annotation { "Feature Type Name" : "Feature", "Feature Type Description" : "" }
export const myFeature = defineFeature(function(context is Context, id is Id, definition is map)
    precondition{}
    {
        {
            var Q0;
            Q0=qCreatedBy(makeId("Top.planeOp"),FACE);
            var sketch = newSketch(context, id + "F0", { "sketchPlane" : qUnion([Q0])});
            skLineSegment(sketch, "E0.bottom", {"start": v(-40.25, 43.5) * mm, "end": v(40.25, 43.5) * mm});
            skLineSegment(sketch, "E0.top", {"start": v(-40.25, -43.5) * mm, "end": v(40.25, -43.5) * mm});
            skLineSegment(sketch, "E0.left", {"start": v(-40.25, 43.5) * mm, "end": v(-40.25, -43.5) * mm});
            skLineSegment(sketch, "E0.right", {"start": v(40.25, 43.5) * mm, "end": v(40.25, -43.5) * mm});
            skSolve(sketch);
        }
        {
            var Q0;
            Q0=qCreatedBy(makeId("Top.planeOp"),FACE);
            var sketch = newSketch(context, id + "F1", { "sketchPlane" : qUnion([Q0])});
            skText(sketch, "E1", { "text": "Toms Cafe", "fontName": "OpenSans-Bold.ttf"});
            skLineSegment(sketch, "E2", {"start": v(-25, -33.55) * mm, "end": v(-40.25, -33.55) * mm, "construction": true});
            skLineSegment(sketch, "E3", {"start": v(25, -33.55) * mm, "end": v(40.25, -33.55) * mm, "construction": true});
            skPoint(sketch, "E4.oppositeSnap0", {"position": v(-32.62, -33.55) * mm});
            skLineSegment(sketch, "E5.bottom", {"start": v(11.82, -37.2) * mm, "end": v(12.9, -37.2) * mm});
            skLineSegment(sketch, "E5.top", {"start": v(11.82, -38.83) * mm, "end": v(12.9, -38.83) * mm});
            skLineSegment(sketch, "E5.left", {"start": v(11.82, -37.2) * mm, "end": v(11.82, -38.83) * mm});
            skLineSegment(sketch, "E5.right", {"start": v(12.9, -37.2) * mm, "end": v(12.9, -38.83) * mm});
            skLineSegment(sketch, "E6.bottom", {"start": v(11.92, -34.98) * mm, "end": v(12.9, -34.98) * mm});
            skLineSegment(sketch, "E6.top", {"start": v(11.92, -36.37) * mm, "end": v(12.9, -36.37) * mm});
            skLineSegment(sketch, "E6.left", {"start": v(11.92, -34.98) * mm, "end": v(11.92, -36.37) * mm});
            skLineSegment(sketch, "E6.right", {"start": v(12.9, -34.98) * mm, "end": v(12.9, -36.37) * mm});
            skLineSegment(sketch, "E7", {"start": v(-39.23, 0) * mm, "end": v(38.52, 0) * mm, "construction": true});
            skCircle(sketch, "E8", {"center": v(-34.75, 38) * mm, "radius": 2.5 * mm});
            skCircle(sketch, "E9", {"center": v(-27.82, 34) * mm, "radius": 2.5 * mm});
            skCircle(sketch, "E10", {"center": v(-34.75, 30) * mm, "radius": 2.5 * mm});
            skCircle(sketch, "E11", {"center": v(-27.82, 26) * mm, "radius": 2.5 * mm});
            skCircle(sketch, "E12.0.1.0", {"center": v(-27.82, 18) * mm, "radius": 2.5 * mm});
            skCircle(sketch, "E12.0.1.1", {"center": v(-34.75, 22) * mm, "radius": 2.5 * mm});
            skCircle(sketch, "E12.0.1.2", {"center": v(-34.75, 14) * mm, "radius": 2.5 * mm});
            skCircle(sketch, "E12.0.1.3", {"center": v(-27.82, 10) * mm, "radius": 2.5 * mm});
            skCircle(sketch, "E12.0.2.0", {"center": v(-27.82, 2) * mm, "radius": 2.5 * mm});
            skCircle(sketch, "E12.0.2.1", {"center": v(-34.75, 6) * mm, "radius": 2.5 * mm});
            skCircle(sketch, "E12.0.2.2", {"center": v(-34.75, -2) * mm, "radius": 2.5 * mm});
            skCircle(sketch, "E12.0.2.3", {"center": v(-27.82, -6) * mm, "radius": 2.5 * mm});
            skCircle(sketch, "E12.0.3.0", {"center": v(-27.82, -14) * mm, "radius": 2.5 * mm});
            skCircle(sketch, "E12.0.3.1", {"center": v(-34.75, -10) * mm, "radius": 2.5 * mm});
            skCircle(sketch, "E12.0.3.2", {"center": v(-34.75, -18) * mm, "radius": 2.5 * mm});
            skCircle(sketch, "E12.0.3.3", {"center": v(-27.82, -22) * mm, "radius": 2.5 * mm});
            skCircle(sketch, "E12.0.4.0", {"center": v(-27.82, -30) * mm, "radius": 2.5 * mm});
            skCircle(sketch, "E12.0.4.1", {"center": v(-34.75, -26) * mm, "radius": 2.5 * mm});
            skCircle(sketch, "E12.0.4.2", {"center": v(-34.75, -34) * mm, "radius": 2.5 * mm});
            skCircle(sketch, "E12.1.0.0", {"center": v(-13.97, 34) * mm, "radius": 2.5 * mm});
            skCircle(sketch, "E12.1.0.1", {"center": v(-20.9, 38) * mm, "radius": 2.5 * mm});
            skCircle(sketch, "E12.1.0.2", {"center": v(-20.9, 30) * mm, "radius": 2.5 * mm});
            skCircle(sketch, "E12.1.0.3", {"center": v(-13.97, 26) * mm, "radius": 2.5 * mm});
            skCircle(sketch, "E12.1.1.0", {"center": v(-13.97, 18) * mm, "radius": 2.5 * mm});
            skCircle(sketch, "E12.1.1.1", {"center": v(-20.9, 22) * mm, "radius": 2.5 * mm});
            skCircle(sketch, "E12.1.1.2", {"center": v(-20.9, 14) * mm, "radius": 2.5 * mm});
            skCircle(sketch, "E12.1.1.3", {"center": v(-13.97, 10) * mm, "radius": 2.5 * mm});
            skCircle(sketch, "E12.1.2.0", {"center": v(-13.97, 2) * mm, "radius": 2.5 * mm});
            skCircle(sketch, "E12.1.2.1", {"center": v(-20.9, 6) * mm, "radius": 2.5 * mm});
            skCircle(sketch, "E12.1.2.2", {"center": v(-20.9, -2) * mm, "radius": 2.5 * mm});
            skCircle(sketch, "E12.1.2.3", {"center": v(-13.97, -6) * mm, "radius": 2.5 * mm});
            skCircle(sketch, "E12.1.3.0", {"center": v(-13.97, -14) * mm, "radius": 2.5 * mm});
            skCircle(sketch, "E12.1.3.1", {"center": v(-20.9, -10) * mm, "radius": 2.5 * mm});
            skCircle(sketch, "E12.1.3.2", {"center": v(-20.9, -18) * mm, "radius": 2.5 * mm});
            skCircle(sketch, "E12.1.3.3", {"center": v(-13.97, -22) * mm, "radius": 2.5 * mm});
            skCircle(sketch, "E12.1.4.0", {"center": v(-13.97, -30) * mm, "radius": 2.5 * mm});
            skCircle(sketch, "E12.1.4.1", {"center": v(-20.9, -26) * mm, "radius": 2.5 * mm});
            skCircle(sketch, "E12.2.0.0", {"center": v(-0.1, 34) * mm, "radius": 2.5 * mm});
            skCircle(sketch, "E12.2.0.1", {"center": v(-7.04, 38) * mm, "radius": 2.5 * mm});
            skCircle(sketch, "E12.2.0.2", {"center": v(-7.04, 30) * mm, "radius": 2.5 * mm});
            skCircle(sketch, "E12.2.0.3", {"center": v(-0.1, 26) * mm, "radius": 2.5 * mm});
            skCircle(sketch, "E12.2.1.0", {"center": v(-0.1, 18) * mm, "radius": 2.5 * mm});
            skCircle(sketch, "E12.2.1.1", {"center": v(-7.04, 22) * mm, "radius": 2.5 * mm});
            skCircle(sketch, "E12.2.1.2", {"center": v(-7.04, 14) * mm, "radius": 2.5 * mm});
            skCircle(sketch, "E12.2.1.3", {"center": v(-0.1, 10) * mm, "radius": 2.5 * mm});
            skCircle(sketch, "E12.2.2.0", {"center": v(-0.1, 2) * mm, "radius": 2.5 * mm});
            skCircle(sketch, "E12.2.2.1", {"center": v(-7.04, 6) * mm, "radius": 2.5 * mm});
            skCircle(sketch, "E12.2.2.2", {"center": v(-7.04, -2) * mm, "radius": 2.5 * mm});
            skCircle(sketch, "E12.2.2.3", {"center": v(-0.1, -6) * mm, "radius": 2.5 * mm});
            skCircle(sketch, "E12.2.3.0", {"center": v(-0.1, -14) * mm, "radius": 2.5 * mm});
            skCircle(sketch, "E12.2.3.1", {"center": v(-7.04, -10) * mm, "radius": 2.5 * mm});
            skCircle(sketch, "E12.2.3.2", {"center": v(-7.04, -18) * mm, "radius": 2.5 * mm});
            skCircle(sketch, "E12.2.3.3", {"center": v(-0.1, -22) * mm, "radius": 2.5 * mm});
            skCircle(sketch, "E12.2.4.0", {"center": v(-0.1, -30) * mm, "radius": 2.5 * mm});
            skCircle(sketch, "E12.2.4.1", {"center": v(-7.04, -26) * mm, "radius": 2.5 * mm});
            skCircle(sketch, "E12.3.0.0", {"center": v(13.75, 34) * mm, "radius": 2.5 * mm});
            skCircle(sketch, "E12.3.0.1", {"center": v(6.82, 38) * mm, "radius": 2.5 * mm});
            skCircle(sketch, "E12.3.0.2", {"center": v(6.82, 30) * mm, "radius": 2.5 * mm});
            skCircle(sketch, "E12.3.0.3", {"center": v(13.75, 26) * mm, "radius": 2.5 * mm});
            skCircle(sketch, "E12.3.1.0", {"center": v(13.75, 18) * mm, "radius": 2.5 * mm});
            skCircle(sketch, "E12.3.1.1", {"center": v(6.82, 22) * mm, "radius": 2.5 * mm});
            skCircle(sketch, "E12.3.1.2", {"center": v(6.82, 14) * mm, "radius": 2.5 * mm});
            skCircle(sketch, "E12.3.1.3", {"center": v(13.75, 10) * mm, "radius": 2.5 * mm});
            skCircle(sketch, "E12.3.2.0", {"center": v(13.75, 2) * mm, "radius": 2.5 * mm});
            skCircle(sketch, "E12.3.2.1", {"center": v(6.82, 6) * mm, "radius": 2.5 * mm});
            skCircle(sketch, "E12.3.2.2", {"center": v(6.82, -2) * mm, "radius": 2.5 * mm});
            skCircle(sketch, "E12.3.2.3", {"center": v(13.75, -6) * mm, "radius": 2.5 * mm});
            skCircle(sketch, "E12.3.3.0", {"center": v(13.75, -14) * mm, "radius": 2.5 * mm});
            skCircle(sketch, "E12.3.3.1", {"center": v(6.82, -10) * mm, "radius": 2.5 * mm});
            skCircle(sketch, "E12.3.3.2", {"center": v(6.82, -18) * mm, "radius": 2.5 * mm});
            skCircle(sketch, "E12.3.3.3", {"center": v(13.75, -22) * mm, "radius": 2.5 * mm});
            skCircle(sketch, "E12.3.4.0", {"center": v(13.75, -30) * mm, "radius": 2.5 * mm});
            skCircle(sketch, "E12.3.4.1", {"center": v(6.82, -26) * mm, "radius": 2.5 * mm});
            skCircle(sketch, "E12.4.0.0", {"center": v(27.6, 34) * mm, "radius": 2.5 * mm});
            skCircle(sketch, "E12.4.0.1", {"center": v(20.67, 38) * mm, "radius": 2.5 * mm});
            skCircle(sketch, "E12.4.0.2", {"center": v(20.67, 30) * mm, "radius": 2.5 * mm});
            skCircle(sketch, "E12.4.0.3", {"center": v(27.6, 26) * mm, "radius": 2.5 * mm});
            skCircle(sketch, "E12.4.1.0", {"center": v(27.6, 18) * mm, "radius": 2.5 * mm});
            skCircle(sketch, "E12.4.1.1", {"center": v(20.67, 22) * mm, "radius": 2.5 * mm});
            skCircle(sketch, "E12.4.1.2", {"center": v(20.67, 14) * mm, "radius": 2.5 * mm});
            skCircle(sketch, "E12.4.1.3", {"center": v(27.6, 10) * mm, "radius": 2.5 * mm});
            skCircle(sketch, "E12.4.2.0", {"center": v(27.6, 2) * mm, "radius": 2.5 * mm});
            skCircle(sketch, "E12.4.2.1", {"center": v(20.67, 6) * mm, "radius": 2.5 * mm});
            skCircle(sketch, "E12.4.2.2", {"center": v(20.67, -2) * mm, "radius": 2.5 * mm});
            skCircle(sketch, "E12.4.2.3", {"center": v(27.6, -6) * mm, "radius": 2.5 * mm});
            skCircle(sketch, "E12.4.3.0", {"center": v(27.6, -14) * mm, "radius": 2.5 * mm});
            skCircle(sketch, "E12.4.3.1", {"center": v(20.67, -10) * mm, "radius": 2.5 * mm});
            skCircle(sketch, "E12.4.3.2", {"center": v(20.67, -18) * mm, "radius": 2.5 * mm});
            skCircle(sketch, "E12.4.3.3", {"center": v(27.6, -22) * mm, "radius": 2.5 * mm});
            skCircle(sketch, "E12.4.4.0", {"center": v(27.6, -30) * mm, "radius": 2.5 * mm});
            skCircle(sketch, "E12.4.4.1", {"center": v(20.67, -26) * mm, "radius": 2.5 * mm});
            skCircle(sketch, "E12.5.0.1", {"center": v(34.53, 38) * mm, "radius": 2.5 * mm});
            skCircle(sketch, "E12.5.0.2", {"center": v(34.53, 30) * mm, "radius": 2.5 * mm});
            skCircle(sketch, "E12.5.1.1", {"center": v(34.53, 22) * mm, "radius": 2.5 * mm});
            skCircle(sketch, "E12.5.1.2", {"center": v(34.53, 14) * mm, "radius": 2.5 * mm});
            skCircle(sketch, "E12.5.2.1", {"center": v(34.53, 6) * mm, "radius": 2.5 * mm});
            skCircle(sketch, "E12.5.2.2", {"center": v(34.53, -2) * mm, "radius": 2.5 * mm});
            skCircle(sketch, "E12.5.3.1", {"center": v(34.53, -10) * mm, "radius": 2.5 * mm});
            skCircle(sketch, "E12.5.3.2", {"center": v(34.53, -18) * mm, "radius": 2.5 * mm});
            skCircle(sketch, "E12.5.4.1", {"center": v(34.53, -26) * mm, "radius": 2.5 * mm});
            skCircle(sketch, "E12.5.4.2", {"center": v(34.53, -34) * mm, "radius": 2.5 * mm});
            skLineSegment(sketch, "E12.direction1", {"start": v(-34.75, 30) * mm, "end": v(-20.9, 30) * mm, "construction": true});
            skLineSegment(sketch, "E12.direction2", {"start": v(-34.75, 30) * mm, "end": v(-34.75, 14) * mm, "construction": true});
            skLineSegment(sketch, "E13", {"start": v(-37.03, 39.03) * mm, "end": v(-40.25, 39.03) * mm, "construction": true});
            skLineSegment(sketch, "E14", {"start": v(37.03, 38) * mm, "end": v(40.25, 38) * mm, "construction": true});
            skLineSegment(sketch, "E15.bottom", {"start": v(-40.25, -43.5) * mm, "end": v(40.25, -43.5) * mm});
            skLineSegment(sketch, "E15.top", {"start": v(-40.25, 43.5) * mm, "end": v(40.25, 43.5) * mm});
            skLineSegment(sketch, "E15.left", {"start": v(-40.25, -43.5) * mm, "end": v(-40.25, 43.5) * mm});
            skLineSegment(sketch, "E15.right", {"start": v(40.25, -43.5) * mm, "end": v(40.25, 43.5) * mm});
            const initialGuessF1  = {"E1": [-0.025, -0.0405, 1, 0, 0.00695]};
            skSetInitialGuess(sketch, initialGuessF1);
            skSolve(sketch);
        }
        {
            var Q0;
            Q0 = qSketchRegion(id + "F1", true);
            extrude(context, id + "F2", {"entities" : qUnion([Q0]), "depth" : 3 * mm, "offsetDistance" : 25 * mm});
        }
        {
            var Q0;
            Q0=makeQuery(id+"F2.opExtrude","CAP_EDGE",EDGE,{"disambiguationData":[OSD([sQuery(id+"F1.wireOp",EDGE,"E15.bottom")])],"isStart":false});
            var Q1;
            Q1=makeQuery(id+"F2.opExtrude","CAP_EDGE",EDGE,{"disambiguationData":[OSD([sQuery(id+"F1.wireOp",EDGE,"E15.left")])],"isStart":false});
            var Q2;
            Q2=makeQuery(id+"F2.opExtrude","CAP_EDGE",EDGE,{"disambiguationData":[OSD([sQuery(id+"F1.wireOp",EDGE,"E15.top")])],"isStart":false});
            var Q3;
            Q3=makeQuery(id+"F2.opExtrude","CAP_EDGE",EDGE,{"disambiguationData":[OSD([sQuery(id+"F1.wireOp",EDGE,"E15.right")])],"isStart":false});
            var Q4;
            Q4=makeQuery(id+"F2.opExtrude","CAP_EDGE",EDGE,{"disambiguationData":[OSD([sQuery(id+"F1.wireOp",EDGE,"E12.0.4.2")])],"isStart":false});
            var Q5;
            Q5=makeQuery(id+"F2.opExtrude","CAP_EDGE",EDGE,{"disambiguationData":[OSD([sQuery(id+"F1.wireOp",EDGE,"E12.0.4.0")])],"isStart":false});
            var Q6;
            Q6=makeQuery(id+"F2.opExtrude","CAP_EDGE",EDGE,{"disambiguationData":[OSD([sQuery(id+"F1.wireOp",EDGE,"E12.0.4.1")])],"isStart":false});
            var Q7;
            Q7=makeQuery(id+"F2.opExtrude","CAP_EDGE",EDGE,{"disambiguationData":[OSD([sQuery(id+"F1.wireOp",EDGE,"E12.0.3.3")])],"isStart":false});
            var Q8;
            Q8=makeQuery(id+"F2.opExtrude","SWEPT_FACE",FACE,{"disambiguationData":[OSD([sQuery(id+"F1.wireOp",EDGE,"E12.0.3.2")])]});
            var Q9;
            Q9=makeQuery(id+"F2.opExtrude","CAP_EDGE",EDGE,{"disambiguationData":[OSD([sQuery(id+"F1.wireOp",EDGE,"E12.0.3.1")])],"isStart":false});
            var Q10;
            Q10=makeQuery(id+"F2.opExtrude","CAP_EDGE",EDGE,{"disambiguationData":[OSD([sQuery(id+"F1.wireOp",EDGE,"E12.0.2.3")])],"isStart":false});
            var Q11;
            Q11=makeQuery(id+"F2.opExtrude","CAP_EDGE",EDGE,{"disambiguationData":[OSD([sQuery(id+"F1.wireOp",EDGE,"E12.0.2.2")])],"isStart":false});
            var Q12;
            Q12=makeQuery(id+"F2.opExtrude","CAP_EDGE",EDGE,{"disambiguationData":[OSD([sQuery(id+"F1.wireOp",EDGE,"E12.0.2.1")])],"isStart":false});
            var Q13;
            Q13=makeQuery(id+"F2.opExtrude","CAP_EDGE",EDGE,{"disambiguationData":[OSD([sQuery(id+"F1.wireOp",EDGE,"E12.0.2.0")])],"isStart":false});
            var Q14;
            Q14=makeQuery(id+"F2.opExtrude","CAP_EDGE",EDGE,{"disambiguationData":[OSD([sQuery(id+"F1.wireOp",EDGE,"E12.0.1.3")])],"isStart":false});
            var Q15;
            Q15=makeQuery(id+"F2.opExtrude","CAP_EDGE",EDGE,{"disambiguationData":[OSD([sQuery(id+"F1.wireOp",EDGE,"E12.0.1.2")])],"isStart":false});
            var Q16;
            Q16=makeQuery(id+"F2.opExtrude","CAP_EDGE",EDGE,{"disambiguationData":[OSD([sQuery(id+"F1.wireOp",EDGE,"E12.0.1.1")])],"isStart":false});
            var Q17;
            Q17=makeQuery(id+"F2.opExtrude","CAP_EDGE",EDGE,{"disambiguationData":[OSD([sQuery(id+"F1.wireOp",EDGE,"E10")])],"isStart":false});
            var Q18;
            Q18=makeQuery(id+"F2.opExtrude","CAP_EDGE",EDGE,{"disambiguationData":[OSD([sQuery(id+"F1.wireOp",EDGE,"E8")])],"isStart":false});
            var Q19;
            Q19=makeQuery(id+"F2.opExtrude","CAP_EDGE",EDGE,{"disambiguationData":[OSD([sQuery(id+"F1.wireOp",EDGE,"E12.0.1.0")])],"isStart":false});
            var Q20;
            Q20=makeQuery(id+"F2.opExtrude","CAP_EDGE",EDGE,{"disambiguationData":[OSD([sQuery(id+"F1.wireOp",EDGE,"E12.0.3.0")])],"isStart":false});
            var Q21;
            Q21=makeQuery(id+"F2.opExtrude","CAP_EDGE",EDGE,{"disambiguationData":[OSD([sQuery(id+"F1.wireOp",EDGE,"E11")])],"isStart":false});
            var Q22;
            Q22=makeQuery(id+"F2.opExtrude","CAP_EDGE",EDGE,{"disambiguationData":[OSD([sQuery(id+"F1.wireOp",EDGE,"E9")])],"isStart":false});
            var Q23;
            Q23=makeQuery(id+"F2.opExtrude","CAP_EDGE",EDGE,{"disambiguationData":[OSD([sQuery(id+"F1.wireOp",EDGE,"E12.1.0.1")])],"isStart":false});
            var Q24;
            Q24=makeQuery(id+"F2.opExtrude","CAP_EDGE",EDGE,{"disambiguationData":[OSD([sQuery(id+"F1.wireOp",EDGE,"E12.1.0.2")])],"isStart":false});
            var Q25;
            Q25=makeQuery(id+"F2.opExtrude","CAP_EDGE",EDGE,{"disambiguationData":[OSD([sQuery(id+"F1.wireOp",EDGE,"E12.1.1.1")])],"isStart":false});
            var Q26;
            Q26=makeQuery(id+"F2.opExtrude","CAP_EDGE",EDGE,{"disambiguationData":[OSD([sQuery(id+"F1.wireOp",EDGE,"E12.1.1.2")])],"isStart":false});
            var Q27;
            Q27=makeQuery(id+"F2.opExtrude","CAP_EDGE",EDGE,{"disambiguationData":[OSD([sQuery(id+"F1.wireOp",EDGE,"E12.1.2.1")])],"isStart":false});
            var Q28;
            Q28=makeQuery(id+"F2.opExtrude","CAP_EDGE",EDGE,{"disambiguationData":[OSD([sQuery(id+"F1.wireOp",EDGE,"E12.1.2.2")])],"isStart":false});
            var Q29;
            Q29=makeQuery(id+"F2.opExtrude","CAP_EDGE",EDGE,{"disambiguationData":[OSD([sQuery(id+"F1.wireOp",EDGE,"E12.1.3.1")])],"isStart":false});
            var Q30;
            Q30=makeQuery(id+"F2.opExtrude","CAP_EDGE",EDGE,{"disambiguationData":[OSD([sQuery(id+"F1.wireOp",EDGE,"E12.1.3.2")])],"isStart":false});
            var Q31;
            Q31=makeQuery(id+"F2.opExtrude","CAP_EDGE",EDGE,{"disambiguationData":[OSD([sQuery(id+"F1.wireOp",EDGE,"E12.1.4.1")])],"isStart":false});
            var Q32;
            Q32=makeQuery(id+"F2.opExtrude","CAP_EDGE",EDGE,{"disambiguationData":[OSD([sQuery(id+"F1.wireOp",EDGE,"E12.1.0.0")])],"isStart":false});
            var Q33;
            Q33=makeQuery(id+"F2.opExtrude","CAP_EDGE",EDGE,{"disambiguationData":[OSD([sQuery(id+"F1.wireOp",EDGE,"E12.1.0.3")])],"isStart":false});
            var Q34;
            Q34=makeQuery(id+"F2.opExtrude","CAP_EDGE",EDGE,{"disambiguationData":[OSD([sQuery(id+"F1.wireOp",EDGE,"E12.1.1.0")])],"isStart":false});
            var Q35;
            Q35=makeQuery(id+"F2.opExtrude","CAP_EDGE",EDGE,{"disambiguationData":[OSD([sQuery(id+"F1.wireOp",EDGE,"E12.1.1.3")])],"isStart":false});
            var Q36;
            Q36=makeQuery(id+"F2.opExtrude","CAP_EDGE",EDGE,{"disambiguationData":[OSD([sQuery(id+"F1.wireOp",EDGE,"E12.1.2.0")])],"isStart":false});
            var Q37;
            Q37=makeQuery(id+"F2.opExtrude","CAP_EDGE",EDGE,{"disambiguationData":[OSD([sQuery(id+"F1.wireOp",EDGE,"E12.1.2.3")])],"isStart":false});
            var Q38;
            Q38=makeQuery(id+"F2.opExtrude","CAP_EDGE",EDGE,{"disambiguationData":[OSD([sQuery(id+"F1.wireOp",EDGE,"E12.1.3.0")])],"isStart":false});
            var Q39;
            Q39=makeQuery(id+"F2.opExtrude","CAP_EDGE",EDGE,{"disambiguationData":[OSD([sQuery(id+"F1.wireOp",EDGE,"E12.1.3.3")])],"isStart":false});
            var Q40;
            Q40=makeQuery(id+"F2.opExtrude","CAP_EDGE",EDGE,{"disambiguationData":[OSD([sQuery(id+"F1.wireOp",EDGE,"E12.1.4.0")])],"isStart":false});
            var Q41;
            Q41=makeQuery(id+"F2.opExtrude","CAP_EDGE",EDGE,{"disambiguationData":[OSD([sQuery(id+"F1.wireOp",EDGE,"E12.2.4.1")])],"isStart":false});
            var Q42;
            Q42=makeQuery(id+"F2.opExtrude","CAP_EDGE",EDGE,{"disambiguationData":[OSD([sQuery(id+"F1.wireOp",EDGE,"E12.2.3.2")])],"isStart":false});
            var Q43;
            Q43=makeQuery(id+"F2.opExtrude","CAP_EDGE",EDGE,{"disambiguationData":[OSD([sQuery(id+"F1.wireOp",EDGE,"E12.2.3.1")])],"isStart":false});
            var Q44;
            Q44=makeQuery(id+"F2.opExtrude","CAP_EDGE",EDGE,{"disambiguationData":[OSD([sQuery(id+"F1.wireOp",EDGE,"E12.2.2.1")])],"isStart":false});
            var Q45;
            Q45=makeQuery(id+"F2.opExtrude","CAP_EDGE",EDGE,{"disambiguationData":[OSD([sQuery(id+"F1.wireOp",EDGE,"E12.2.1.2")])],"isStart":false});
            var Q46;
            Q46=makeQuery(id+"F2.opExtrude","CAP_EDGE",EDGE,{"disambiguationData":[OSD([sQuery(id+"F1.wireOp",EDGE,"E12.2.1.1")])],"isStart":false});
            var Q47;
            Q47=makeQuery(id+"F2.opExtrude","CAP_EDGE",EDGE,{"disambiguationData":[OSD([sQuery(id+"F1.wireOp",EDGE,"E12.2.0.2")])],"isStart":false});
            var Q48;
            Q48=makeQuery(id+"F2.opExtrude","CAP_EDGE",EDGE,{"disambiguationData":[OSD([sQuery(id+"F1.wireOp",EDGE,"E12.2.0.1")])],"isStart":false});
            var Q49;
            Q49=makeQuery(id+"F2.opExtrude","CAP_EDGE",EDGE,{"disambiguationData":[OSD([sQuery(id+"F1.wireOp",EDGE,"E12.2.0.0")])],"isStart":false});
            var Q50;
            Q50=makeQuery(id+"F2.opExtrude","CAP_EDGE",EDGE,{"disambiguationData":[OSD([sQuery(id+"F1.wireOp",EDGE,"E12.2.0.3")])],"isStart":false});
            var Q51;
            Q51=makeQuery(id+"F2.opExtrude","CAP_EDGE",EDGE,{"disambiguationData":[OSD([sQuery(id+"F1.wireOp",EDGE,"E12.2.1.0")])],"isStart":false});
            var Q52;
            Q52=makeQuery(id+"F2.opExtrude","CAP_EDGE",EDGE,{"disambiguationData":[OSD([sQuery(id+"F1.wireOp",EDGE,"E12.2.1.3")])],"isStart":false});
            var Q53;
            Q53=makeQuery(id+"F2.opExtrude","CAP_EDGE",EDGE,{"disambiguationData":[OSD([sQuery(id+"F1.wireOp",EDGE,"E12.2.2.0")])],"isStart":false});
            var Q54;
            Q54=makeQuery(id+"F2.opExtrude","CAP_EDGE",EDGE,{"disambiguationData":[OSD([sQuery(id+"F1.wireOp",EDGE,"E12.2.2.2")])],"isStart":false});
            var Q55;
            Q55=makeQuery(id+"F2.opExtrude","CAP_EDGE",EDGE,{"disambiguationData":[OSD([sQuery(id+"F1.wireOp",EDGE,"E12.2.2.3")])],"isStart":false});
            var Q56;
            Q56=makeQuery(id+"F2.opExtrude","CAP_EDGE",EDGE,{"disambiguationData":[OSD([sQuery(id+"F1.wireOp",EDGE,"E12.2.3.0")])],"isStart":false});
            var Q57;
            Q57=makeQuery(id+"F2.opExtrude","CAP_EDGE",EDGE,{"disambiguationData":[OSD([sQuery(id+"F1.wireOp",EDGE,"E12.2.3.3")])],"isStart":false});
            var Q58;
            Q58=makeQuery(id+"F2.opExtrude","CAP_EDGE",EDGE,{"disambiguationData":[OSD([sQuery(id+"F1.wireOp",EDGE,"E12.2.4.0")])],"isStart":false});
            var Q59;
            Q59=makeQuery(id+"F2.opExtrude","CAP_EDGE",EDGE,{"disambiguationData":[OSD([sQuery(id+"F1.wireOp",EDGE,"E12.3.0.1")])],"isStart":false});
            var Q60;
            Q60=makeQuery(id+"F2.opExtrude","CAP_EDGE",EDGE,{"disambiguationData":[OSD([sQuery(id+"F1.wireOp",EDGE,"E12.3.0.2")])],"isStart":false});
            chamfer(context, id + "F3", {"entities" : qUnion([Q0, Q1, Q2, Q3, Q4, Q5, Q6, Q7, Q8, Q9, Q10, Q11, Q12, Q13, Q14, Q15, Q16, Q17, Q18, Q19, Q20, Q21, Q22, Q23, Q24, Q25, Q26, Q27, Q28, Q29, Q30, Q31, Q32, Q33, Q34, Q35, Q36, Q37, Q38, Q39, Q40, Q41, Q42, Q43, Q44, Q45, Q46, Q47, Q48, Q49, Q50, Q51, Q52, Q53, Q54, Q55, Q56, Q57, Q58, Q59, Q60]), "width" : 1 * mm, "tangentPropagation" : true});
        }
        {
            var Q0;
            Q0=makeQuery(id+"F2.opExtrude","CAP_EDGE",EDGE,{"disambiguationData":[OSD([sQuery(id+"F1.wireOp",EDGE,"E12.3.1.1")])],"isStart":false});
            var Q1;
            Q1=makeQuery(id+"F2.opExtrude","CAP_EDGE",EDGE,{"disambiguationData":[OSD([sQuery(id+"F1.wireOp",EDGE,"E12.3.1.2")])],"isStart":false});
            var Q2;
            Q2=makeQuery(id+"F2.opExtrude","CAP_EDGE",EDGE,{"disambiguationData":[OSD([sQuery(id+"F1.wireOp",EDGE,"E12.3.2.1")])],"isStart":false});
            var Q3;
            Q3=makeQuery(id+"F2.opExtrude","CAP_EDGE",EDGE,{"disambiguationData":[OSD([sQuery(id+"F1.wireOp",EDGE,"E12.3.2.2")])],"isStart":false});
            var Q4;
            Q4=makeQuery(id+"F2.opExtrude","CAP_EDGE",EDGE,{"disambiguationData":[OSD([sQuery(id+"F1.wireOp",EDGE,"E12.3.3.1")])],"isStart":false});
            var Q5;
            Q5=makeQuery(id+"F2.opExtrude","CAP_EDGE",EDGE,{"disambiguationData":[OSD([sQuery(id+"F1.wireOp",EDGE,"E12.3.3.2")])],"isStart":false});
            var Q6;
            Q6=makeQuery(id+"F2.opExtrude","CAP_EDGE",EDGE,{"disambiguationData":[OSD([sQuery(id+"F1.wireOp",EDGE,"E12.3.4.1")])],"isStart":false});
            var Q7;
            Q7=makeQuery(id+"F2.opExtrude","CAP_EDGE",EDGE,{"disambiguationData":[OSD([sQuery(id+"F1.wireOp",EDGE,"E12.3.4.0")])],"isStart":false});
            var Q8;
            Q8=makeQuery(id+"F2.opExtrude","CAP_EDGE",EDGE,{"disambiguationData":[OSD([sQuery(id+"F1.wireOp",EDGE,"E12.3.3.3")])],"isStart":false});
            var Q9;
            Q9=makeQuery(id+"F2.opExtrude","CAP_EDGE",EDGE,{"disambiguationData":[OSD([sQuery(id+"F1.wireOp",EDGE,"E12.3.3.0")])],"isStart":false});
            var Q10;
            Q10=makeQuery(id+"F2.opExtrude","CAP_EDGE",EDGE,{"disambiguationData":[OSD([sQuery(id+"F1.wireOp",EDGE,"E12.3.2.3")])],"isStart":false});
            var Q11;
            Q11=makeQuery(id+"F2.opExtrude","CAP_EDGE",EDGE,{"disambiguationData":[OSD([sQuery(id+"F1.wireOp",EDGE,"E12.3.2.0")])],"isStart":false});
            var Q12;
            Q12=makeQuery(id+"F2.opExtrude","CAP_EDGE",EDGE,{"disambiguationData":[OSD([sQuery(id+"F1.wireOp",EDGE,"E12.3.1.3")])],"isStart":false});
            var Q13;
            Q13=makeQuery(id+"F2.opExtrude","CAP_EDGE",EDGE,{"disambiguationData":[OSD([sQuery(id+"F1.wireOp",EDGE,"E12.3.1.0")])],"isStart":false});
            var Q14;
            Q14=makeQuery(id+"F2.opExtrude","CAP_EDGE",EDGE,{"disambiguationData":[OSD([sQuery(id+"F1.wireOp",EDGE,"E12.3.0.3")])],"isStart":false});
            var Q15;
            Q15=makeQuery(id+"F2.opExtrude","CAP_EDGE",EDGE,{"disambiguationData":[OSD([sQuery(id+"F1.wireOp",EDGE,"E12.3.0.0")])],"isStart":false});
            var Q16;
            Q16=makeQuery(id+"F2.opExtrude","CAP_EDGE",EDGE,{"disambiguationData":[OSD([sQuery(id+"F1.wireOp",EDGE,"E12.4.0.1")])],"isStart":false});
            var Q17;
            Q17=makeQuery(id+"F2.opExtrude","CAP_EDGE",EDGE,{"disambiguationData":[OSD([sQuery(id+"F1.wireOp",EDGE,"E12.4.0.2")])],"isStart":false});
            var Q18;
            Q18=makeQuery(id+"F2.opExtrude","CAP_EDGE",EDGE,{"disambiguationData":[OSD([sQuery(id+"F1.wireOp",EDGE,"E12.4.1.1")])],"isStart":false});
            var Q19;
            Q19=makeQuery(id+"F2.opExtrude","CAP_EDGE",EDGE,{"disambiguationData":[OSD([sQuery(id+"F1.wireOp",EDGE,"E12.4.1.2")])],"isStart":false});
            var Q20;
            Q20=makeQuery(id+"F2.opExtrude","CAP_EDGE",EDGE,{"disambiguationData":[OSD([sQuery(id+"F1.wireOp",EDGE,"E12.4.2.1")])],"isStart":false});
            var Q21;
            Q21=makeQuery(id+"F2.opExtrude","CAP_EDGE",EDGE,{"disambiguationData":[OSD([sQuery(id+"F1.wireOp",EDGE,"E12.4.2.2")])],"isStart":false});
            var Q22;
            Q22=makeQuery(id+"F2.opExtrude","CAP_EDGE",EDGE,{"disambiguationData":[OSD([sQuery(id+"F1.wireOp",EDGE,"E12.4.3.1")])],"isStart":false});
            var Q23;
            Q23=makeQuery(id+"F2.opExtrude","CAP_EDGE",EDGE,{"disambiguationData":[OSD([sQuery(id+"F1.wireOp",EDGE,"E12.4.3.2")])],"isStart":false});
            var Q24;
            Q24=makeQuery(id+"F2.opExtrude","CAP_EDGE",EDGE,{"disambiguationData":[OSD([sQuery(id+"F1.wireOp",EDGE,"E12.4.4.1")])],"isStart":false});
            var Q25;
            Q25=makeQuery(id+"F2.opExtrude","CAP_EDGE",EDGE,{"disambiguationData":[OSD([sQuery(id+"F1.wireOp",EDGE,"E12.4.0.0")])],"isStart":false});
            var Q26;
            Q26=makeQuery(id+"F2.opExtrude","CAP_EDGE",EDGE,{"disambiguationData":[OSD([sQuery(id+"F1.wireOp",EDGE,"E12.4.0.3")])],"isStart":false});
            var Q27;
            Q27=makeQuery(id+"F2.opExtrude","CAP_EDGE",EDGE,{"disambiguationData":[OSD([sQuery(id+"F1.wireOp",EDGE,"E12.4.1.0")])],"isStart":false});
            var Q28;
            Q28=makeQuery(id+"F2.opExtrude","CAP_EDGE",EDGE,{"disambiguationData":[OSD([sQuery(id+"F1.wireOp",EDGE,"E12.4.1.3")])],"isStart":false});
            var Q29;
            Q29=makeQuery(id+"F2.opExtrude","CAP_EDGE",EDGE,{"disambiguationData":[OSD([sQuery(id+"F1.wireOp",EDGE,"E12.4.2.0")])],"isStart":false});
            var Q30;
            Q30=makeQuery(id+"F2.opExtrude","CAP_EDGE",EDGE,{"disambiguationData":[OSD([sQuery(id+"F1.wireOp",EDGE,"E12.4.2.3")])],"isStart":false});
            var Q31;
            Q31=makeQuery(id+"F2.opExtrude","CAP_EDGE",EDGE,{"disambiguationData":[OSD([sQuery(id+"F1.wireOp",EDGE,"E12.4.3.0")])],"isStart":false});
            var Q32;
            Q32=makeQuery(id+"F2.opExtrude","CAP_EDGE",EDGE,{"disambiguationData":[OSD([sQuery(id+"F1.wireOp",EDGE,"E12.4.3.3")])],"isStart":false});
            var Q33;
            Q33=makeQuery(id+"F2.opExtrude","CAP_EDGE",EDGE,{"disambiguationData":[OSD([sQuery(id+"F1.wireOp",EDGE,"E12.4.4.0")])],"isStart":false});
            var Q34;
            Q34=makeQuery(id+"F2.opExtrude","CAP_EDGE",EDGE,{"disambiguationData":[OSD([sQuery(id+"F1.wireOp",EDGE,"E12.5.4.2")])],"isStart":false});
            var Q35;
            Q35=makeQuery(id+"F2.opExtrude","CAP_EDGE",EDGE,{"disambiguationData":[OSD([sQuery(id+"F1.wireOp",EDGE,"E12.5.4.1")])],"isStart":false});
            var Q36;
            Q36=makeQuery(id+"F2.opExtrude","CAP_EDGE",EDGE,{"disambiguationData":[OSD([sQuery(id+"F1.wireOp",EDGE,"E12.5.3.2")])],"isStart":false});
            var Q37;
            Q37=makeQuery(id+"F2.opExtrude","CAP_EDGE",EDGE,{"disambiguationData":[OSD([sQuery(id+"F1.wireOp",EDGE,"E12.5.3.1")])],"isStart":false});
            var Q38;
            Q38=makeQuery(id+"F2.opExtrude","CAP_EDGE",EDGE,{"disambiguationData":[OSD([sQuery(id+"F1.wireOp",EDGE,"E12.5.2.2")])],"isStart":false});
            var Q39;
            Q39=makeQuery(id+"F2.opExtrude","CAP_EDGE",EDGE,{"disambiguationData":[OSD([sQuery(id+"F1.wireOp",EDGE,"E12.5.2.1")])],"isStart":false});
            var Q40;
            Q40=makeQuery(id+"F2.opExtrude","CAP_EDGE",EDGE,{"disambiguationData":[OSD([sQuery(id+"F1.wireOp",EDGE,"E12.5.1.2")])],"isStart":false});
            var Q41;
            Q41=makeQuery(id+"F2.opExtrude","CAP_EDGE",EDGE,{"disambiguationData":[OSD([sQuery(id+"F1.wireOp",EDGE,"E12.5.1.1")])],"isStart":false});
            var Q42;
            Q42=makeQuery(id+"F2.opExtrude","CAP_EDGE",EDGE,{"disambiguationData":[OSD([sQuery(id+"F1.wireOp",EDGE,"E12.5.0.2")])],"isStart":false});
            var Q43;
            Q43=makeQuery(id+"F2.opExtrude","CAP_EDGE",EDGE,{"disambiguationData":[OSD([sQuery(id+"F1.wireOp",EDGE,"E12.5.0.1")])],"isStart":false});
            chamfer(context, id + "F4", {"entities" : qUnion([Q0, Q1, Q2, Q3, Q4, Q5, Q6, Q7, Q8, Q9, Q10, Q11, Q12, Q13, Q14, Q15, Q16, Q17, Q18, Q19, Q20, Q21, Q22, Q23, Q24, Q25, Q26, Q27, Q28, Q29, Q30, Q31, Q32, Q33, Q34, Q35, Q36, Q37, Q38, Q39, Q40, Q41, Q42, Q43]), "width" : 1 * mm, "tangentPropagation" : true});
        }
    });